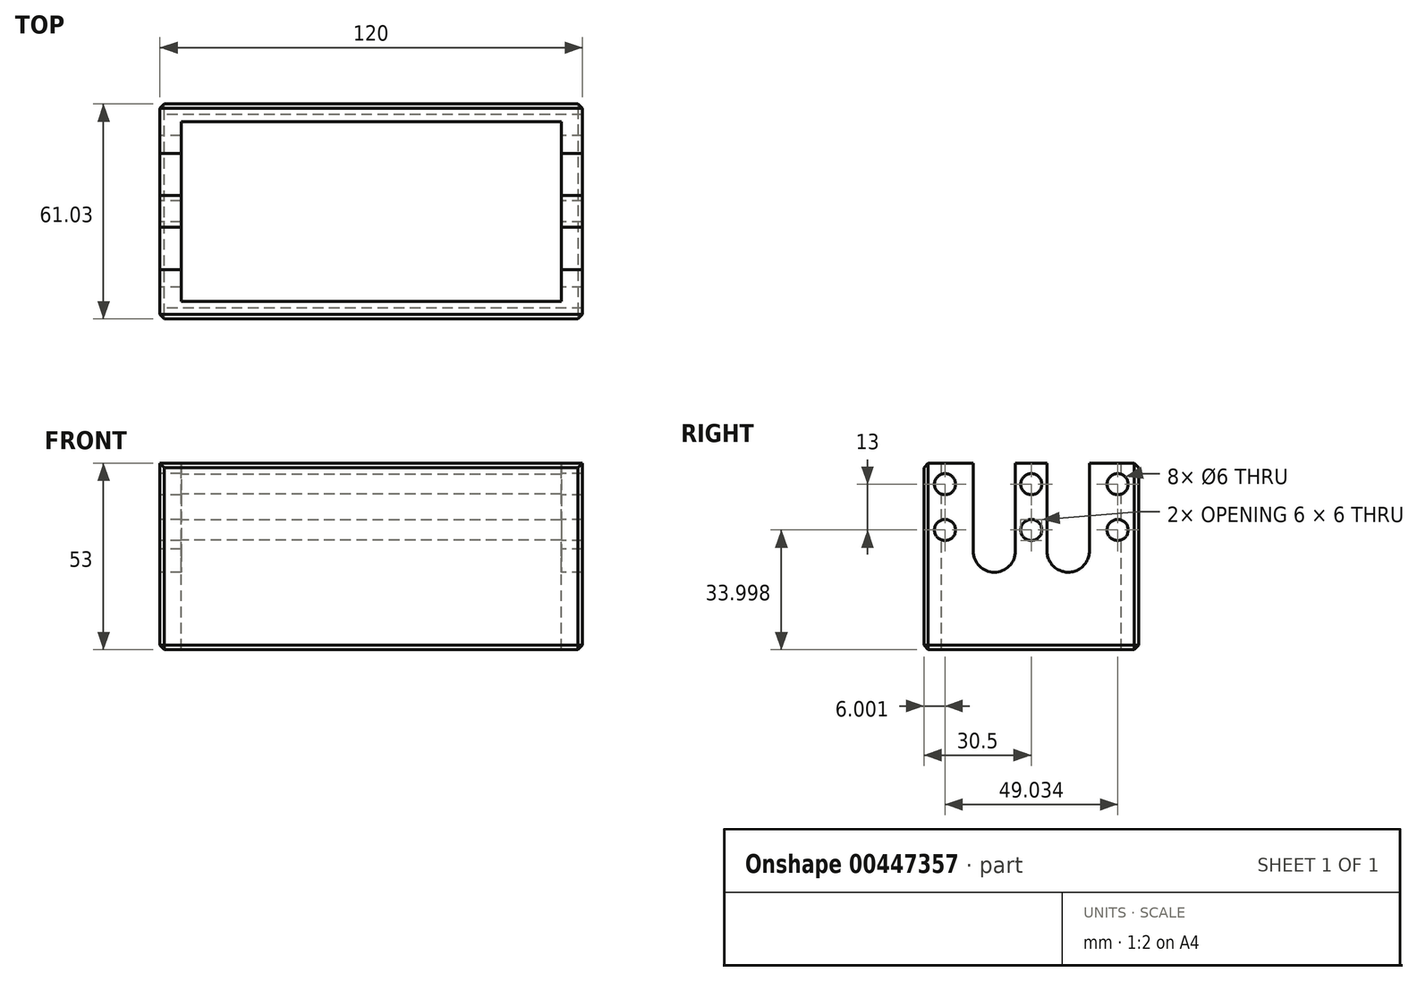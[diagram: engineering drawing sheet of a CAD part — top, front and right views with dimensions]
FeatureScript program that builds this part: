
annotation { "Feature Type Name" : "Feature", "Feature Type Description" : "" }
export const myFeature = defineFeature(function(context is Context, id is Id, definition is map)
    precondition{}
    {
        {
            var Q0;
            Q0=qCreatedBy(makeId("Right.planeOp"),FACE);
            var sketch = newSketch(context, id + "F0", { "sketchPlane" : qUnion([Q0])});
            skLineSegment(sketch, "E0", {"start": v(-22.05, 27.56) * mm, "end": v(-22.05, -25.44) * mm});
            skLineSegment(sketch, "E1", {"start": v(-22.05, -25.44) * mm, "end": v(38.98, -25.44) * mm});
            skLineSegment(sketch, "E2", {"start": v(38.98, -25.44) * mm, "end": v(38.98, 27.56) * mm});
            skArc(sketch, "E3", {"start": v(-8.05, 2.56) * mm, "mid": v(-2.05, -3.44) * mm, "end": v(3.95, 2.56) * mm});
            skArc(sketch, "E4", {"start": v(12.95, 3.12) * mm, "mid": v(18.65, -3.45) * mm, "end": v(24.95, 2.55) * mm});
            skLineSegment(sketch, "E5", {"start": v(-8.05, 2.56) * mm, "end": v(-8.05, 27.56) * mm});
            skLineSegment(sketch, "E6", {"start": v(3.95, 2.56) * mm, "end": v(3.95, 27.56) * mm});
            skLineSegment(sketch, "E7", {"start": v(12.95, 3.12) * mm, "end": v(12.95, 27.56) * mm});
            skLineSegment(sketch, "E8", {"start": v(24.95, 2.55) * mm, "end": v(24.98, 27.56) * mm});
            skLineSegment(sketch, "E9", {"start": v(-22.05, 27.56) * mm, "end": v(-8.05, 27.56) * mm});
            skLineSegment(sketch, "E10", {"start": v(3.95, 27.56) * mm, "end": v(12.95, 27.56) * mm});
            skLineSegment(sketch, "E11", {"start": v(24.98, 27.56) * mm, "end": v(38.98, 27.56) * mm});
            skCircle(sketch, "E12", {"center": v(-16.05, 21.56) * mm, "radius": 3 * mm});
            skCircle(sketch, "E13", {"center": v(-16.05, 8.56) * mm, "radius": 3 * mm});
            skCircle(sketch, "E14", {"center": v(8.45, 21.56) * mm, "radius": 3 * mm});
            skCircle(sketch, "E15", {"center": v(8.45, 8.56) * mm, "radius": 3 * mm});
            skCircle(sketch, "E16", {"center": v(32.98, 21.56) * mm, "radius": 3 * mm});
            skCircle(sketch, "E17", {"center": v(32.98, 8.56) * mm, "radius": 3 * mm});
            skLineSegment(sketch, "E18", {"start": v(8.45, 38.54) * mm, "end": v(8.45, -33.25) * mm, "construction": true});
            skPoint(sketch, "E18.startSnap0", {"position": v(8.45, 27.56) * mm});
            skCircle(sketch, "E19", {"center": v(-2.05, 2.56) * mm, "radius": 11 * mm, "construction": true});
            skCircle(sketch, "E20", {"center": v(18.94, 2.56) * mm, "radius": 11 * mm, "construction": true});
            skSolve(sketch);
        }
        {
            var Q0;
            Q0=makeQuery(id+"F0.imprint","IMPRINT",FACE,{"disambiguationData":[TD([[makeQuery(id+"F0.imprint","IMPRINT",EDGE,{"derivedFrom":sQuery(id+"F0.wireOp",EDGE,"E0")}),1.0]])]});
            extrude(context, id + "F1", {"entities" : qUnion([Q0]), "depth" : 120 * mm});
        }
        {
            var Q0;
            Q0=makeQuery(id+"F1.opExtrude","SWEPT_FACE",FACE,{"disambiguationData":[OSD([sQuery(id+"F0.wireOp",EDGE,"E11")])]});
            var sketch = newSketch(context, id + "F2", { "sketchPlane" : qUnion([Q0])});
            skLineSegment(sketch, "E21.bottom", {"start": v(6, 33.98) * mm, "end": v(114, 33.98) * mm});
            skLineSegment(sketch, "E21.top", {"start": v(6, -17.05) * mm, "end": v(114, -17.05) * mm});
            skLineSegment(sketch, "E21.left", {"start": v(6, 33.98) * mm, "end": v(6, -17.05) * mm});
            skLineSegment(sketch, "E21.right", {"start": v(114, 33.98) * mm, "end": v(114, -17.05) * mm});
            skSolve(sketch);
        }
        {
            var Q0;
            Q0 = qSketchRegion(id + "F2", true);
            extrude(context, id + "F3", {"entities" : qUnion([Q0]), "operationType" : NewBodyOperationType.REMOVE, "oppositeDirection" : true, "depth" : 80 * mm});
        }
        {
            var Q0;
            Q0=makeQuery(id+"F1.opExtrude","CAP_EDGE",EDGE,{"disambiguationData":[OSD([sQuery(id+"F0.wireOp",EDGE,"E2")])],"isStart":true});
            var Q1;
            Q1=makeQuery(id+"F1.opExtrude","CAP_EDGE",EDGE,{"disambiguationData":[OSD([sQuery(id+"F0.wireOp",EDGE,"E0")])],"isStart":true});
            var Q2;
            Q2=makeQuery(id+"F1.opExtrude","SWEPT_FACE",FACE,{"disambiguationData":[OSD([sQuery(id+"F0.wireOp",EDGE,"E0")])]});
            var Q3;
            Q3=makeQuery(id+"F1.opExtrude","SWEPT_FACE",FACE,{"disambiguationData":[OSD([sQuery(id+"F0.wireOp",EDGE,"E2")])]});
            var Q4;
            Q4=makeQuery(id+"F1.opExtrude","CAP_EDGE",EDGE,{"disambiguationData":[OSD([sQuery(id+"F0.wireOp",EDGE,"E1")])],"isStart":false});
            var Q5;
            Q5=makeQuery(id+"F1.opExtrude","CAP_EDGE",EDGE,{"disambiguationData":[OSD([sQuery(id+"F0.wireOp",EDGE,"E1")])],"isStart":true});
            chamfer(context, id + "F4", {"entities" : qUnion([Q0, Q1, Q2, Q3, Q4, Q5]), "width" : 1.25 * mm, "tangentPropagation" : true});
        }
    });
